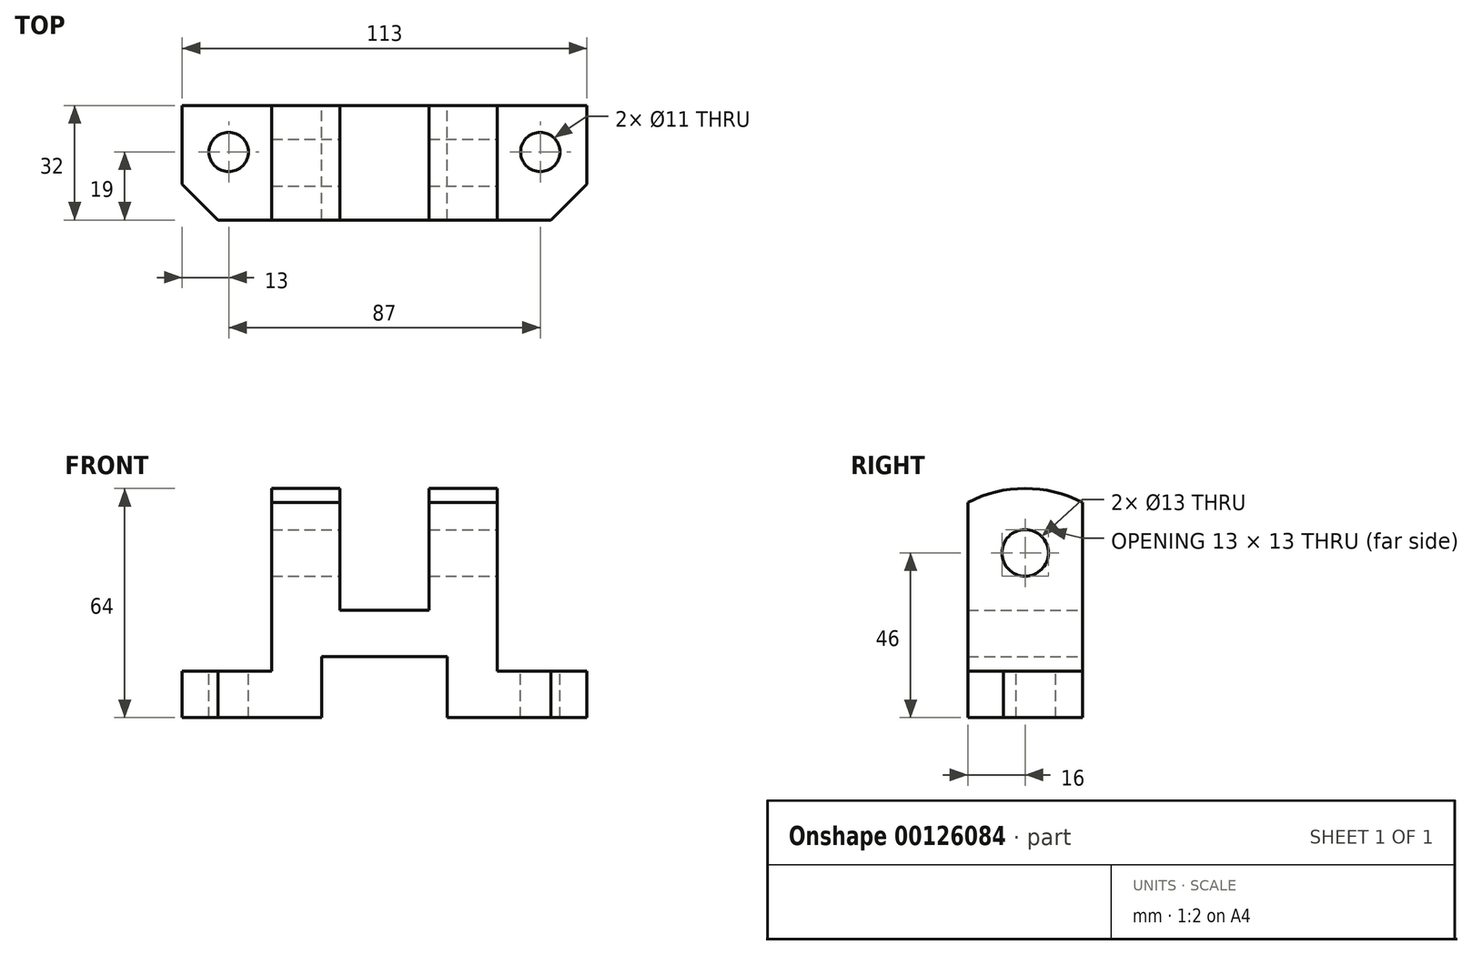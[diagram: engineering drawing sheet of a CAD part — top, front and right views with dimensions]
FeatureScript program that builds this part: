
annotation { "Feature Type Name" : "Feature", "Feature Type Description" : "" }
export const myFeature = defineFeature(function(context is Context, id is Id, definition is map)
    precondition{}
    {
        {
            var Q0;
            Q0=qCreatedBy(makeId("Front.planeOp"),FACE);
            var sketch = newSketch(context, id + "F0", { "sketchPlane" : qUnion([Q0])});
            skLineSegment(sketch, "E0", {"start": v(0, 0) * mm, "end": v(17.5, 0) * mm, "construction": true});
            skLineSegment(sketch, "E1", {"start": v(0, 0) * mm, "end": v(-17.5, 0) * mm, "construction": true});
            skLineSegment(sketch, "E2", {"start": v(-17.5, 0) * mm, "end": v(-56.5, 0) * mm});
            skLineSegment(sketch, "E3", {"start": v(-56.5, 0) * mm, "end": v(-56.5, 13) * mm});
            skLineSegment(sketch, "E4", {"start": v(-56.5, 13) * mm, "end": v(-31.5, 13) * mm});
            skLineSegment(sketch, "E5", {"start": v(-31.5, 13) * mm, "end": v(-31.5, 60.13) * mm});
            skLineSegment(sketch, "E6", {"start": v(-31.5, 60.13) * mm, "end": v(-12.5, 60.13) * mm});
            skLineSegment(sketch, "E7", {"start": v(-12.5, 60.13) * mm, "end": v(-12.5, 30) * mm});
            skLineSegment(sketch, "E8", {"start": v(-12.5, 30) * mm, "end": v(12.5, 30) * mm});
            skLineSegment(sketch, "E9", {"start": v(12.5, 30) * mm, "end": v(12.5, 60.13) * mm});
            skLineSegment(sketch, "E10", {"start": v(12.5, 60.13) * mm, "end": v(31.5, 60.13) * mm});
            skLineSegment(sketch, "E11", {"start": v(31.5, 60.13) * mm, "end": v(31.5, 13) * mm});
            skLineSegment(sketch, "E12", {"start": v(31.5, 13) * mm, "end": v(56.5, 13) * mm});
            skLineSegment(sketch, "E13", {"start": v(56.5, 13) * mm, "end": v(56.5, 0) * mm});
            skLineSegment(sketch, "E14", {"start": v(56.5, 0) * mm, "end": v(17.5, 0) * mm});
            skLineSegment(sketch, "E15", {"start": v(-17.5, 0) * mm, "end": v(-17.5, 17) * mm});
            skLineSegment(sketch, "E16", {"start": v(17.5, 0) * mm, "end": v(17.5, 17) * mm});
            skLineSegment(sketch, "E17", {"start": v(17.5, 17) * mm, "end": v(-17.5, 17) * mm});
            skSolve(sketch);
        }
        {
            var Q0;
            Q0 = qSketchRegion(id + "F0", true);
            extrude(context, id + "F1", {"entities" : qUnion([Q0]), "endBound" : BoundingType.SYMMETRIC, "depth" : 32 * mm});
        }
        {
            var Q0;
            Q0=makeQuery(id+"F1.opExtrude","CAP_EDGE",EDGE,{"disambiguationData":[OSD([sQuery(id+"F0.wireOp",EDGE,"E13")])],"isStart":false});
            chamfer(context, id + "F2", {"entities" : qUnion([Q0]), "width" : 10 * mm, "tangentPropagation" : true});
        }
        {
            var Q0;
            Q0=makeQuery(id+"F1.opExtrude","CAP_EDGE",EDGE,{"disambiguationData":[OSD([sQuery(id+"F0.wireOp",EDGE,"E3")])],"isStart":false});
            chamfer(context, id + "F3", {"entities" : qUnion([Q0]), "width" : 10 * mm, "tangentPropagation" : true});
        }
        {
            var Q0;
            Q0=makeQuery(id+"F1.opExtrude","SWEPT_FACE",FACE,{"disambiguationData":[OSD([sQuery(id+"F0.wireOp",EDGE,"E12")])]});
            var sketch = newSketch(context, id + "F4", { "sketchPlane" : qUnion([Q0])});
            skLineSegment(sketch, "E18", {"start": v(56.5, 3) * mm, "end": v(43.5, 3) * mm, "construction": true});
            skLineSegment(sketch, "E19", {"start": v(43.5, 3) * mm, "end": v(43.5, 16) * mm, "construction": true});
            skCircle(sketch, "E20", {"center": v(43.5, 3) * mm, "radius": 5.5 * mm});
            skLineSegment(sketch, "E21", {"start": v(43.5, 3) * mm, "end": v(-43.5, 3) * mm, "construction": true});
            skCircle(sketch, "E22", {"center": v(-43.5, 3) * mm, "radius": 5.5 * mm});
            skSolve(sketch);
        }
        {
            var Q0;
            Q0 = qSketchRegion(id + "F4", true);
            var Q1;
            Q1=makeQuery(id+"F1.opExtrude","SWEPT_FACE",FACE,{"disambiguationData":[OSD([sQuery(id+"F0.wireOp",EDGE,"E2")])]});
            extrude(context, id + "F5", {"entities" : qUnion([Q0]), "operationType" : NewBodyOperationType.REMOVE, "endBound" : BoundingType.UP_TO_SURFACE, "oppositeDirection" : true, "endBoundEntityFace" : qUnion([Q1]), "depth" : 25 * mm});
        }
        {
            var Q0;
            Q0=makeQuery(id+"F1.opExtrude","SWEPT_FACE",FACE,{"disambiguationData":[OSD([sQuery(id+"F0.wireOp",EDGE,"E11")])]});
            var sketch = newSketch(context, id + "F6", { "sketchPlane" : qUnion([Q0])});
            skLineSegment(sketch, "E23", {"start": v(0, 0) * mm, "end": v(0, 46) * mm, "construction": true});
            skCircle(sketch, "E24", {"center": v(0, 46) * mm, "radius": 6.5 * mm});
            skSolve(sketch);
        }
        {
            var Q0;
            Q0 = qSketchRegion(id + "F6", true);
            var Q1;
            Q1=makeQuery(id+"F1.opExtrude","SWEPT_FACE",FACE,{"disambiguationData":[OSD([sQuery(id+"F0.wireOp",EDGE,"E5")])]});
            extrude(context, id + "F7", {"entities" : qUnion([Q0]), "operationType" : NewBodyOperationType.REMOVE, "endBound" : BoundingType.UP_TO_SURFACE, "oppositeDirection" : true, "endBoundEntityFace" : qUnion([Q1]), "depth" : 25 * mm});
        }
        {
            var Q0;
            Q0=makeQuery(id+"F1.opExtrude","SWEPT_FACE",FACE,{"disambiguationData":[OSD([sQuery(id+"F0.wireOp",EDGE,"E11")])]});
            var sketch = newSketch(context, id + "F8", { "sketchPlane" : qUnion([Q0])});
            skArc(sketch, "E25", {"start": v(16, 60.13) * mm, "mid": v(0, 64) * mm, "end": v(-16, 60.13) * mm});
            skLineSegment(sketch, "E26", {"start": v(16, 60.13) * mm, "end": v(-16, 60.13) * mm});
            skSolve(sketch);
        }
        {
            var Q0;
            Q0 = qSketchRegion(id + "F8", true);
            extrude(context, id + "F9", {"entities" : qUnion([Q0]), "operationType" : NewBodyOperationType.ADD, "oppositeDirection" : true, "depth" : 19 * mm});
        }
        {
            var Q0;
            Q0=makeQuery(id+"F1.opExtrude","SWEPT_FACE",FACE,{"disambiguationData":[OSD([sQuery(id+"F0.wireOp",EDGE,"E5")])]});
            var sketch = newSketch(context, id + "F10", { "sketchPlane" : qUnion([Q0])});
            skArc(sketch, "E27", {"start": v(16, 60.13) * mm, "mid": v(0, 64) * mm, "end": v(-16, 60.13) * mm});
            skLineSegment(sketch, "E28", {"start": v(16, 60.13) * mm, "end": v(-16, 60.13) * mm});
            skSolve(sketch);
        }
        {
            var Q0;
            Q0 = qSketchRegion(id + "F10", true);
            extrude(context, id + "F11", {"entities" : qUnion([Q0]), "operationType" : NewBodyOperationType.ADD, "oppositeDirection" : true, "depth" : 19 * mm});
        }
    });
